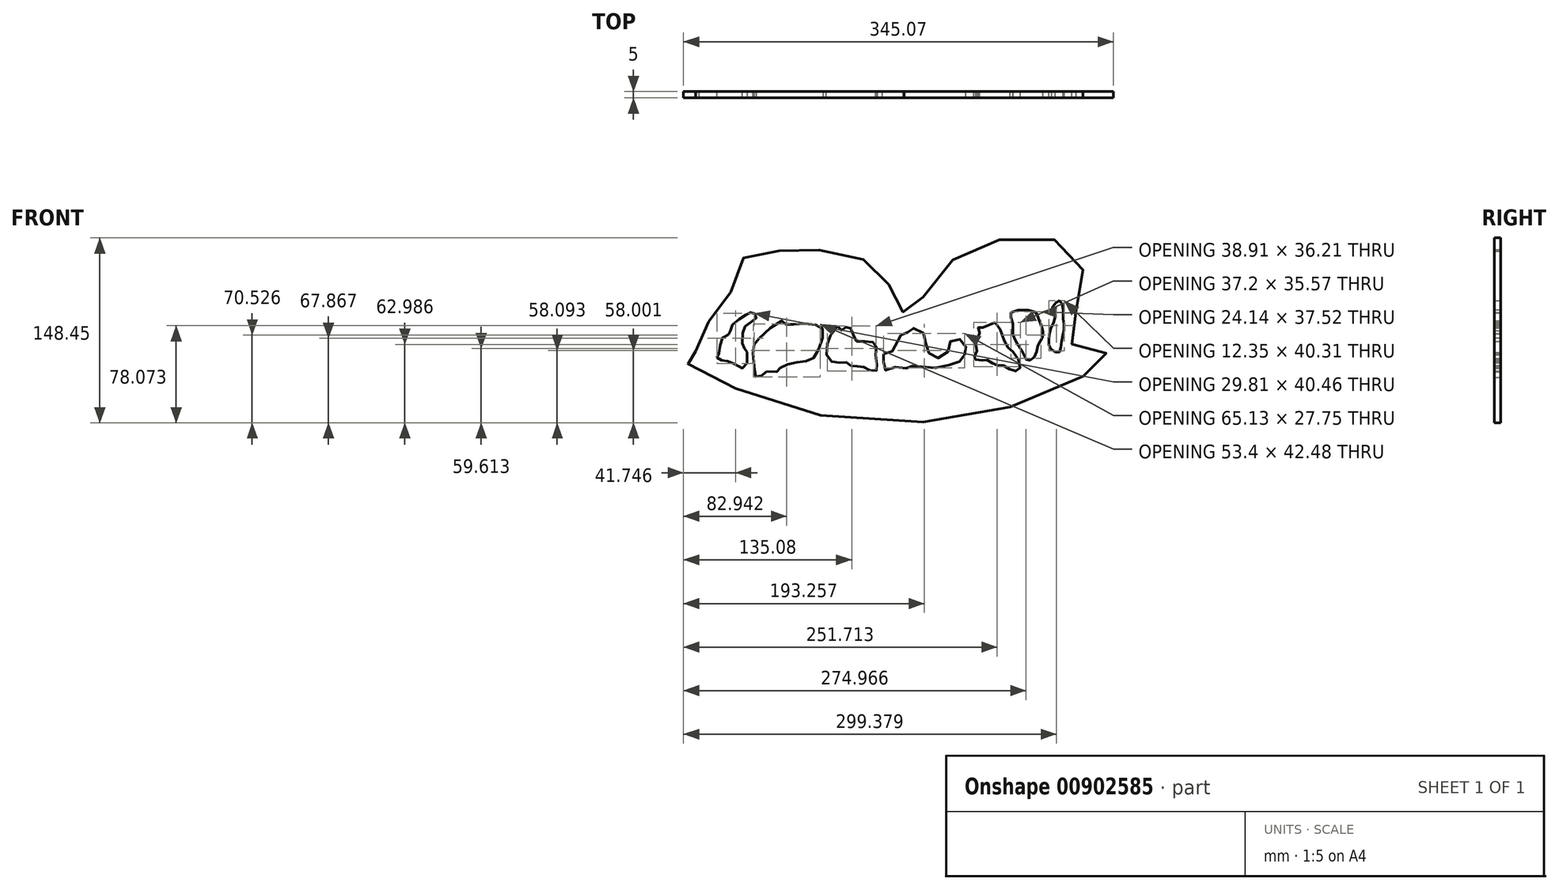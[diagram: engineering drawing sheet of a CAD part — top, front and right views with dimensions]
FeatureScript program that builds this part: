
annotation { "Feature Type Name" : "Feature", "Feature Type Description" : "" }
export const myFeature = defineFeature(function(context is Context, id is Id, definition is map)
    precondition{}
    {
        {
            var Q0;
            Q0=qCreatedBy(makeId("Front.planeOp"),FACE);
            var sketch = newSketch(context, id + "F0", { "sketchPlane" : qUnion([Q0])});
            skLineSegment(sketch, "E0.bottom", {"start": v(200, 200) * mm, "end": v(-200, 200) * mm});
            skLineSegment(sketch, "E0.top", {"start": v(200, -200) * mm, "end": v(-200, -200) * mm});
            skLineSegment(sketch, "E0.left", {"start": v(200, 200) * mm, "end": v(200, -200) * mm});
            skLineSegment(sketch, "E0.right", {"start": v(-200, 200) * mm, "end": v(-200, -200) * mm});
            skPoint(sketch, "E0.middle", {"position": v(0, 0) * mm});
            skSolve(sketch);
        }
        {
            var Q0;
            Q0 = qSketchRegion(id + "F0", true);
            extrude(context, id + "F1", {"entities" : qUnion([Q0]), "depth" : 5 * mm, "offsetDistance" : 25 * mm});
        }
        {
            var Q0;
            Q0=makeQuery(id+"F1.opExtrude","CAP_FACE",FACE,{"disambiguationData":[OSD([sQuery(id+"F0.wireOp",EDGE,"E0.bottom"),sQuery(id+"F0.wireOp",EDGE,"E0.top"),sQuery(id+"F0.wireOp",EDGE,"E0.left"),sQuery(id+"F0.wireOp",EDGE,"E0.right")])],"isStart":false});
            var sketch = newSketch(context, id + "F2", { "sketchPlane" : qUnion([Q0])});
            skFitSpline(sketch, "E1", {"points": [v(-158.6, -13.96) * mm, v(-153.66, 0) * mm, v(-149.42, 8.32) * mm, v(-141.64, 16.8) * mm, v(-131.74, 31.3) * mm, v(-124.32, 46.85) * mm, v(-121.13, 59.58) * mm, v(-111.94, 65.94) * mm, v(-93.2, 66.65) * mm, v(-75.17, 65.94) * mm, v(-56.08, 67.36) * mm, v(-30.63, 62.76) * mm, v(-17.2, 54.28) * mm, v(-7.65, 44.38) * mm, v(1.5, 33.61) * mm, v(8.43, 24.57) * mm, v(7.8, 16.38) * mm, v(17.05, 26.26) * mm, v(22.3, 28.15) * mm, v(37.64, 48.3) * mm, v(52.85, 63.14) * mm, v(82.19, 74.8) * mm, v(116.48, 76.57) * mm, v(144.41, 69.86) * mm, v(152.19, 50.41) * mm, v(146.89, 27.43) * mm, v(146.18, 10.82) * mm, v(143.35, 0) * mm, v(143.7, -8.98) * mm, v(151.13, -12.52) * mm, v(171.28, -15.7) * mm, v(176.58, -17.82) * mm, v(141.46, -39.49) * mm, v(74.87, -63.86) * mm, v(-29.18, -69.8) * mm, v(-124.91, -44.84) * mm, v(-154.64, -28.19) * mm, v(-168.31, -21.65) * mm, v(-156.5, -18.03) * mm, v(-158.6, -13.96) * mm]});
            skFitSpline(sketch, "E2", {"points": [v(-141.64, -19.08) * mm, v(-139.67, -15.3) * mm, v(-137.56, -3.52) * mm, v(-131.26, 0) * mm, v(-130.42, 5.1) * mm, v(-121.59, 13.08) * mm, v(-115.5, 16.8) * mm, v(-112.13, 16.8) * mm, v(-109.82, 13.08) * mm, v(-116.75, 7.62) * mm, v(-120.54, 1.94) * mm, v(-120.33, -11.3) * mm, v(-118.43, -11.93) * mm, v(-118.86, -27.07) * mm, v(-129.58, -23.25) * mm, v(-136.3, -21.6) * mm, v(-141.64, -19.08) * mm]});
            skFitSpline(sketch, "E3", {"points": [v(-108.02, -3.83) * mm, v(-89, 10.44) * mm, v(-86.32, 7.46) * mm, v(-78, 7.76) * mm, v(-63.73, 7.46) * mm, v(-56.6, 3.6) * mm, v(-58.97, -9.48) * mm, v(-64.91, -20.18) * mm, v(-73.24, -22.56) * mm, v(-83.64, -24.35) * mm, v(-91.08, -27.91) * mm, v(-93.2, -30.5) * mm, v(-103.22, -30.71) * mm, v(-106.8, -34.7) * mm, v(-111.21, -33.87) * mm, v(-111.42, -27.14) * mm, v(-112.68, -19.36) * mm, v(-111.84, -9.27) * mm, v(-108.02, -3.83) * mm]});
            skFitSpline(sketch, "E4", {"points": [v(-45.05, 6.18) * mm, v(-41.26, 2.6) * mm, v(-36.85, 6.18) * mm, v(-32.43, 0) * mm, v(-29.91, -5.8) * mm, v(-19.61, -6.02) * mm, v(-13.72, -9.48) * mm, v(-14.36, -19.36) * mm, v(-13.1, -29.14) * mm, v(-19.61, -29.14) * mm, v(-25.92, -25.99) * mm, v(-32.67, -26.3) * mm, v(-36.97, -23.25) * mm, v(-44, -23.25) * mm, v(-52.82, -19.36) * mm, v(-51.35, -2.65) * mm, v(-48.18, 1.51) * mm, v(-45.05, 6.18) * mm]});
            skFitSpline(sketch, "E5", {"points": [v(-7.79, -16.43) * mm, v(-2.95, -16.43) * mm, v(7.14, 0) * mm, v(10.71, 0) * mm, v(13.45, 4.39) * mm, v(17.23, 3.96) * mm, v(24.59, 0) * mm, v(26.06, -8.65) * mm, v(28.37, -15.16) * mm, v(34.26, -19.58) * mm, v(43.3, -15.58) * mm, v(44.98, -7.8) * mm, v(49.81, -3.4) * mm, v(57.8, -8.23) * mm, v(58.01, -11.8) * mm, v(57.17, -16.43) * mm, v(55.07, -21.26) * mm, v(48.13, -23.57) * mm, v(38.04, -27.36) * mm, v(23.54, -26.52) * mm, v(18.28, -26.3) * mm, v(13.24, -25.89) * mm, v(10.5, -27.57) * mm, v(2.93, -26.52) * mm, v(-5.9, -29.88) * mm, v(-6.74, -24.83) * mm, v(-8.84, -20.63) * mm, v(-7.79, -16.43) * mm]});
            skFitSpline(sketch, "E6", {"points": [v(81.72, 9.23) * mm, v(90.47, -8.77) * mm, v(95.72, -14.02) * mm, v(101.72, -27.52) * mm, v(96.22, -29.88) * mm, v(88.22, -25.52) * mm, v(82.22, -25.27) * mm, v(75.47, -21.02) * mm, v(70.97, -21.52) * mm, v(64.47, -19.77) * mm, v(66.97, -14.77) * mm, v(66.22, -6.27) * mm, v(69.22, 0) * mm, v(68.22, 5.23) * mm, v(73.72, 5.23) * mm, v(81.72, 9.23) * mm]});
            skFitSpline(sketch, "E7", {"points": [v(94.42, 17.14) * mm, v(95.9, 8.51) * mm, v(95.9, 0) * mm, v(100.36, -9.32) * mm, v(105.12, -17.35) * mm, v(107.5, -21.51) * mm, v(113.44, -18.54) * mm, v(116.12, -9.03) * mm, v(119.39, -3.08) * mm, v(119.1, 5.84) * mm, v(115.82, 13.86) * mm, v(113.74, 17.73) * mm, v(94.42, 17.14) * mm]});
            skFitSpline(sketch, "E8", {"points": [v(133.28, 26.69) * mm, v(128.87, 22.9) * mm, v(126.97, 18.91) * mm, v(129.92, 14.29) * mm, v(126.34, 4.4) * mm, v(124.66, -6.31) * mm, v(126.55, -12.52) * mm, v(133.07, -14.72) * mm, v(134.75, -7.16) * mm, v(137.06, 4.2) * mm, v(136.22, 13.03) * mm, v(136.22, 20.17) * mm, v(133.28, 26.69) * mm]});
            skSolve(sketch);
        }
        {
            var Q0;
            Q0=makeQuery(id+"F2.imprint","IMPRINT",FACE,{"disambiguationData":[TD([[makeQuery(id+"F2.imprint","IMPRINT",EDGE,{"derivedFrom":sQuery(id+"F2.wireOp",EDGE,"E1")}),1.0]])]});
            extrude(context, id + "F3", {"entities" : qUnion([Q0]), "operationType" : NewBodyOperationType.REMOVE, "endBound" : BoundingType.UP_TO_NEXT, "oppositeDirection" : true, "depth" : 25 * mm, "offsetDistance" : 25 * mm});
        }
        {
            var Q0;
            Q0=makeQuery(id+"F2.imprint","IMPRINT",FACE,{"disambiguationData":[TD([[makeQuery(id+"F2.imprint","IMPRINT",EDGE,{"derivedFrom":sQuery(id+"F2.wireOp",EDGE,"E2")}),-1.0]])]});
            var Q1;
            Q1=makeQuery(id+"F2.imprint","IMPRINT",FACE,{"disambiguationData":[TD([[makeQuery(id+"F2.imprint","IMPRINT",EDGE,{"derivedFrom":sQuery(id+"F2.wireOp",EDGE,"E3")}),-1.0]])]});
            var Q2;
            Q2=makeQuery(id+"F2.imprint","IMPRINT",FACE,{"disambiguationData":[TD([[makeQuery(id+"F2.imprint","IMPRINT",EDGE,{"derivedFrom":sQuery(id+"F2.wireOp",EDGE,"E4")}),-1.0]])]});
            var Q3;
            Q3=makeQuery(id+"F2.imprint","IMPRINT",FACE,{"disambiguationData":[TD([[makeQuery(id+"F2.imprint","IMPRINT",EDGE,{"derivedFrom":sQuery(id+"F2.wireOp",EDGE,"E5")}),-1.0]])]});
            var Q4;
            Q4=makeQuery(id+"F2.imprint","IMPRINT",FACE,{"disambiguationData":[TD([[makeQuery(id+"F2.imprint","IMPRINT",EDGE,{"derivedFrom":sQuery(id+"F2.wireOp",EDGE,"E6")}),-1.0]])]});
            var Q5;
            Q5=makeQuery(id+"F2.imprint","IMPRINT",FACE,{"disambiguationData":[TD([[makeQuery(id+"F2.imprint","IMPRINT",EDGE,{"derivedFrom":sQuery(id+"F2.wireOp",EDGE,"E7")}),1.0]])]});
            var Q6;
            Q6=makeQuery(id+"F2.imprint","IMPRINT",FACE,{"disambiguationData":[TD([[makeQuery(id+"F2.imprint","IMPRINT",EDGE,{"derivedFrom":sQuery(id+"F2.wireOp",EDGE,"E8")}),1.0]])]});
            extrude(context, id + "F4", {"entities" : qUnion([Q0, Q1, Q2, Q3, Q4, Q5, Q6]), "operationType" : NewBodyOperationType.REMOVE, "oppositeDirection" : true, "depth" : 25 * mm, "offsetDistance" : 25 * mm});
        }
    });
